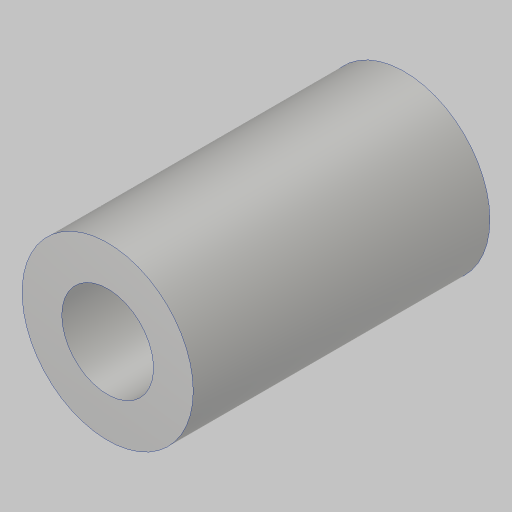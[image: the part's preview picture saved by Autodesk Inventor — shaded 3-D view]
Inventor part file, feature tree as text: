
AUTODESK INVENTOR PART (.ipt)
format: ipt  version: 2023.5 (Build 275446000, 446)  size: 172,544 bytes
history: native  units: in
note: dims shown in document units (in); Inventor stores cm internally (conversion verified against a paired STEP export)
features: extrude x1, hole x1
ambient origin geometry x8: Origin, YZ Plane, XZ Plane, XY Plane, X Axis, Y Axis, Z Axis, Center Point
bodies: Solid1 (feature_tree)
feature tree (2):
  extrude  "Extrusion1"  Depth=0.65in
  hole  "Hole1"  [1 undecoded]
note: 1 required parameter value undecoded (feature->parameter linkage not recoverable at this tier; creation-order binding heuristic only, values carry confidence <= 0.55)
